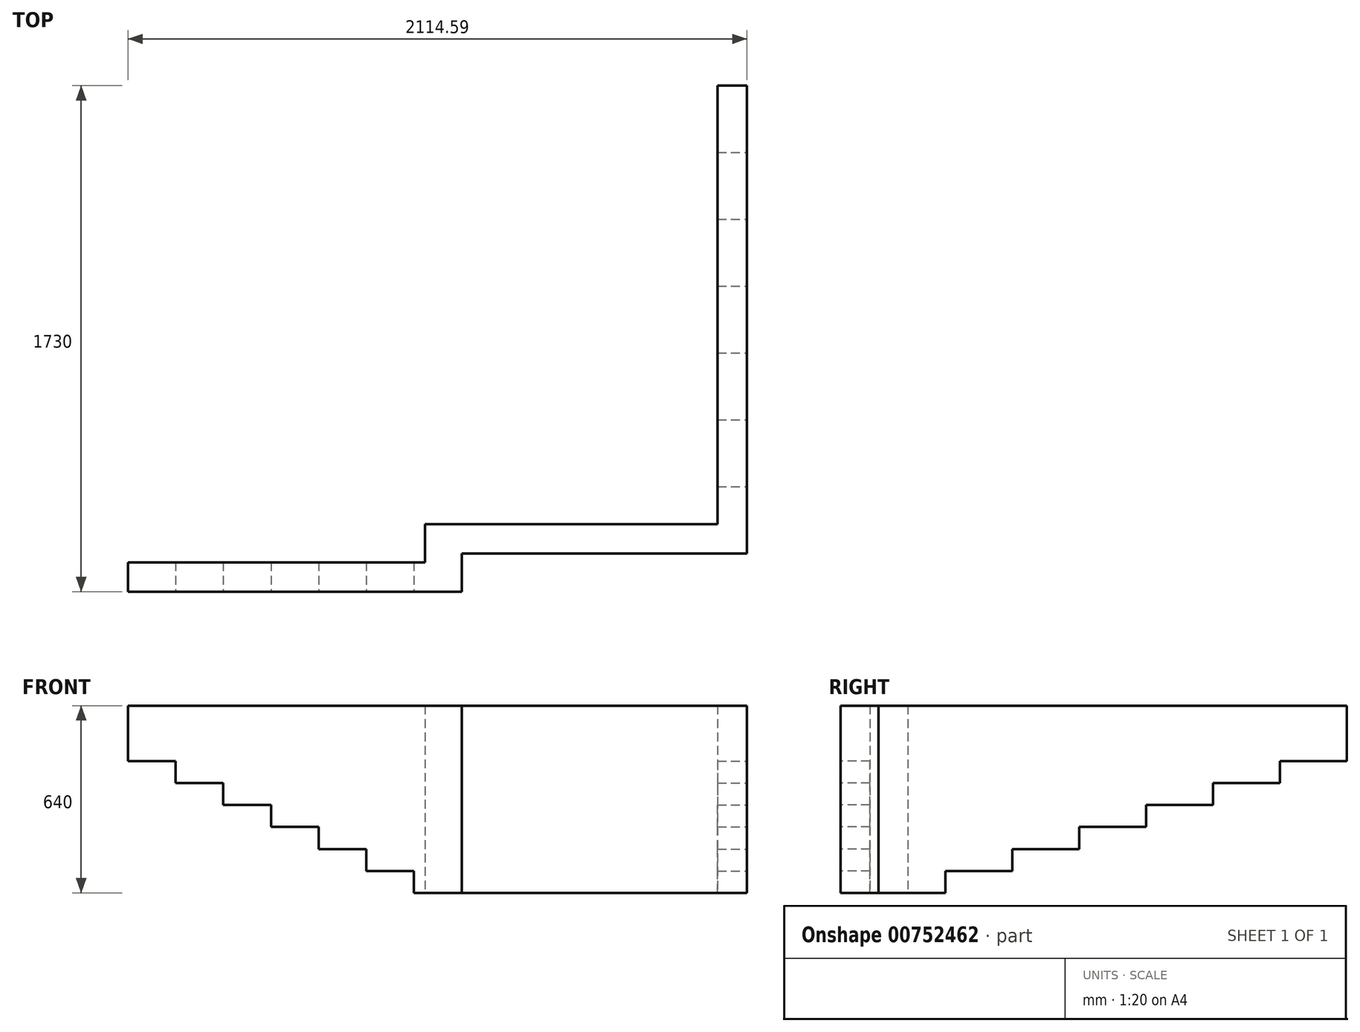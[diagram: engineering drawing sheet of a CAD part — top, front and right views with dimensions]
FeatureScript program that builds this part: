
annotation { "Feature Type Name" : "Feature", "Feature Type Description" : "" }
export const myFeature = defineFeature(function(context is Context, id is Id, definition is map)
    precondition{}
    {
        {
            var Q0;
            Q0=qCreatedBy(makeId("Top.planeOp"),FACE);
            var sketch = newSketch(context, id + "F0", { "sketchPlane" : qUnion([Q0])});
            skLineSegment(sketch, "E0.bottom", {"start": v(0, 0) * mm, "end": v(1140, 0) * mm});
            skLineSegment(sketch, "E0.top", {"start": v(0, 100) * mm, "end": v(1140, 100) * mm});
            skLineSegment(sketch, "E0.left", {"start": v(0, 0) * mm, "end": v(0, 100) * mm});
            skLineSegment(sketch, "E0.right", {"start": v(1140, 0) * mm, "end": v(1140, 100) * mm});
            skLineSegment(sketch, "E1.bottom", {"start": v(1014.6, 230) * mm, "end": v(2114.6, 230) * mm});
            skLineSegment(sketch, "E1.top", {"start": v(1014.6, 130) * mm, "end": v(2114.6, 130) * mm});
            skLineSegment(sketch, "E1.left", {"start": v(1014.6, 230) * mm, "end": v(1014.6, 130) * mm});
            skLineSegment(sketch, "E1.right", {"start": v(2114.6, 230) * mm, "end": v(2114.6, 130) * mm});
            skLineSegment(sketch, "E2.bottom", {"start": v(2114.6, 230) * mm, "end": v(2014.6, 230) * mm});
            skLineSegment(sketch, "E2.top", {"start": v(2114.6, 1730) * mm, "end": v(2014.6, 1730) * mm});
            skLineSegment(sketch, "E2.left", {"start": v(2114.6, 230) * mm, "end": v(2114.6, 1730) * mm});
            skLineSegment(sketch, "E2.right", {"start": v(2014.6, 230) * mm, "end": v(2014.6, 1730) * mm});
            skLineSegment(sketch, "E3.bottom", {"start": v(1014.6, 130) * mm, "end": v(1140, 130) * mm});
            skLineSegment(sketch, "E3.top", {"start": v(1014.6, 100) * mm, "end": v(1140, 100) * mm});
            skLineSegment(sketch, "E3.left", {"start": v(1014.6, 130) * mm, "end": v(1014.6, 100) * mm});
            skLineSegment(sketch, "E3.right", {"start": v(1140, 130) * mm, "end": v(1140, 100) * mm});
            skSolve(sketch);
        }
        {
            var Q0;
            Q0 = qSketchRegion(id + "F0", true);
            extrude(context, id + "F1", {"entities" : qUnion([Q0]), "depth" : (4 * 160) * mm, "offsetDistance" : 25 * mm});
        }
        {
            var Q0;
            Q0=makeQuery(id+"F1.opExtrude","SWEPT_FACE",FACE,{"disambiguationData":[OSD([sQuery(id+"F0.wireOp",EDGE,"E0.bottom")])]});
            var sketch = newSketch(context, id + "F2", { "sketchPlane" : qUnion([Q0])});
            skLineSegment(sketch, "E4", {"start": v(0, 450) * mm, "end": v(162.86, 450) * mm});
            skLineSegment(sketch, "E5", {"start": v(162.86, 450) * mm, "end": v(162.86, 375) * mm});
            skLineSegment(sketch, "E6", {"start": v(162.86, 375) * mm, "end": v(325.71, 375) * mm});
            skLineSegment(sketch, "E7", {"start": v(325.71, 375) * mm, "end": v(325.71, 300) * mm});
            skLineSegment(sketch, "E8", {"start": v(325.71, 300) * mm, "end": v(488.57, 300) * mm});
            skLineSegment(sketch, "E9", {"start": v(488.57, 300) * mm, "end": v(488.57, 225) * mm});
            skLineSegment(sketch, "E10", {"start": v(488.57, 225) * mm, "end": v(651.43, 225) * mm});
            skLineSegment(sketch, "E11", {"start": v(651.43, 225) * mm, "end": v(651.43, 150) * mm});
            skLineSegment(sketch, "E12", {"start": v(651.43, 150) * mm, "end": v(814.29, 150) * mm});
            skLineSegment(sketch, "E13", {"start": v(814.29, 150) * mm, "end": v(814.29, 75) * mm});
            skLineSegment(sketch, "E14", {"start": v(814.29, 75) * mm, "end": v(977.14, 75) * mm});
            skLineSegment(sketch, "E15", {"start": v(977.14, 75) * mm, "end": v(977.14, 0) * mm});
            skLineSegment(sketch, "E16", {"start": v(977.14, 0) * mm, "end": v(1140, 0) * mm});
            skSolve(sketch);
        }
        {
            var Q0;
            Q0 = qSketchRegion(id + "F2", true);
            var Q1;
            {var subQ0=sQuery(id+"F2.wireOp",EDGE,"E4");Q1=makeQuery(id+"F2.imprint","IMPRINT",FACE,{"disambiguationData":[TD([[makeQuery(id+"F2.imprint","IMPRINT",EDGE,{"derivedFrom":subQ0}),-1.0]])]});}
            extrude(context, id + "F3", {"entities" : qUnion([Q0, Q1]), "operationType" : NewBodyOperationType.REMOVE, "endBound" : BoundingType.THROUGH_ALL, "oppositeDirection" : true, "depth" : 25 * mm, "offsetDistance" : 25 * mm});
        }
        {
            var Q0;
            Q0=makeQuery(id+"F1.opExtrude","SWEPT_FACE",FACE,{"disambiguationData":[OSD([sQuery(id+"F0.wireOp",EDGE,"E1.right"),sQuery(id+"F0.wireOp",EDGE,"E2.left")])]});
            var sketch = newSketch(context, id + "F4", { "sketchPlane" : qUnion([Q0])});
            skLineSegment(sketch, "E17", {"start": v(1272.86, 300) * mm, "end": v(1044.29, 300) * mm});
            skLineSegment(sketch, "E18", {"start": v(1044.29, 300) * mm, "end": v(1044.29, 225) * mm});
            skLineSegment(sketch, "E19", {"start": v(1044.29, 225) * mm, "end": v(815.71, 225) * mm});
            skLineSegment(sketch, "E20", {"start": v(815.71, 225) * mm, "end": v(815.71, 150) * mm});
            skLineSegment(sketch, "E21", {"start": v(815.71, 150) * mm, "end": v(587.14, 150) * mm});
            skLineSegment(sketch, "E22", {"start": v(587.14, 150) * mm, "end": v(587.14, 75) * mm});
            skLineSegment(sketch, "E23", {"start": v(587.14, 75) * mm, "end": v(358.57, 75) * mm});
            skLineSegment(sketch, "E24", {"start": v(358.57, 75) * mm, "end": v(358.57, 0) * mm});
            skLineSegment(sketch, "E25", {"start": v(358.57, 0) * mm, "end": v(130, 0) * mm});
            skLineSegment(sketch, "E26", {"start": v(1272.86, 300) * mm, "end": v(1272.86, 375) * mm});
            skLineSegment(sketch, "E27", {"start": v(1272.86, 375) * mm, "end": v(1501.43, 375) * mm});
            skLineSegment(sketch, "E28", {"start": v(1501.43, 375) * mm, "end": v(1501.43, 450) * mm});
            skLineSegment(sketch, "E29", {"start": v(1501.43, 450) * mm, "end": v(1730, 450) * mm});
            skSolve(sketch);
        }
        {
            var Q0;
            Q0 = qSketchRegion(id + "F4", true);
            var Q1;
            Q1=makeQuery(id+"F4.imprint","IMPRINT",FACE,{"disambiguationData":[TD([[makeQuery(id+"F4.imprint","IMPRINT",EDGE,{"derivedFrom":sQuery(id+"F4.wireOp",EDGE,"E17")}),1.0]])]});
            extrude(context, id + "F5", {"entities" : qUnion([Q0, Q1]), "operationType" : NewBodyOperationType.REMOVE, "endBound" : BoundingType.THROUGH_ALL, "oppositeDirection" : true, "depth" : 25 * mm, "offsetDistance" : 25 * mm});
        }
    });
